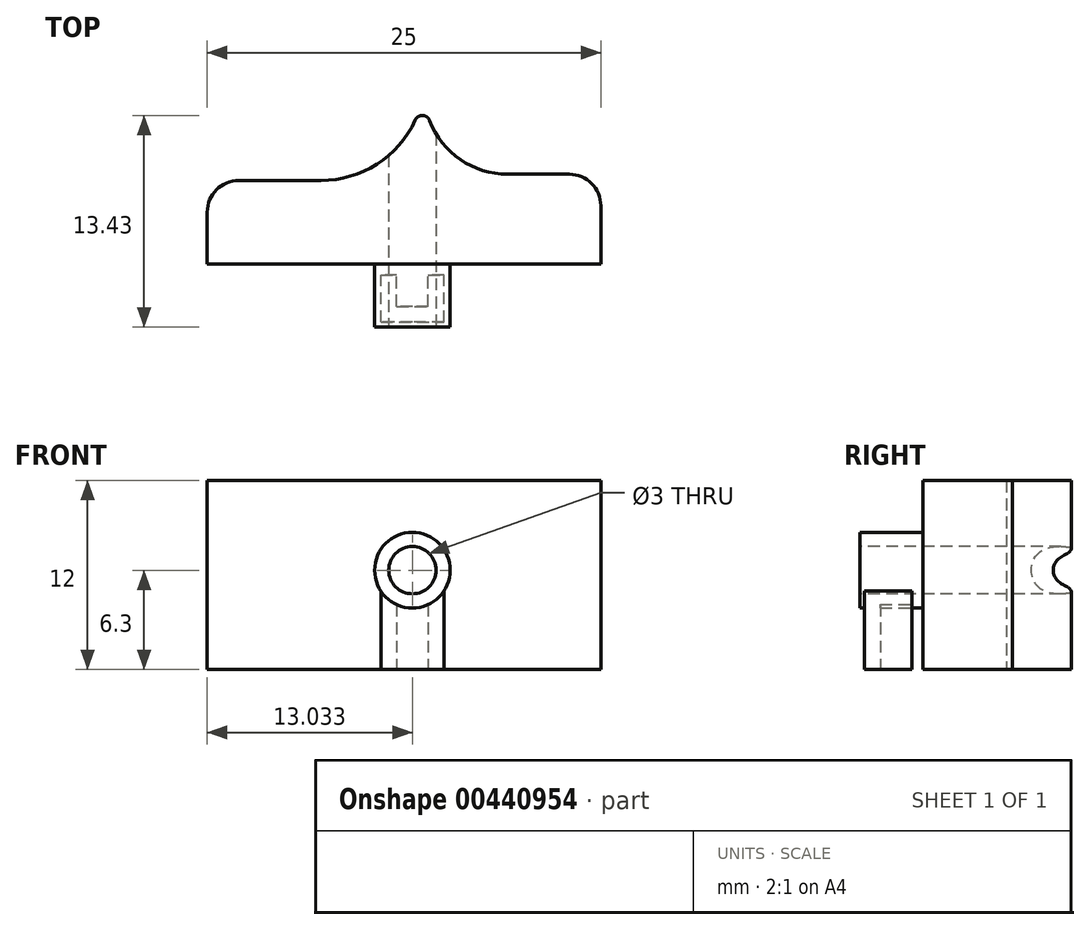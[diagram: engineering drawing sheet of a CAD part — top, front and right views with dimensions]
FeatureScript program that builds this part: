
annotation { "Feature Type Name" : "Feature", "Feature Type Description" : "" }
export const myFeature = defineFeature(function(context is Context, id is Id, definition is map)
    precondition{}
    {
        {
            var Q0;
            Q0=qCreatedBy(makeId("Top.planeOp"),FACE);
            var sketch = newSketch(context, id + "F0", { "sketchPlane" : qUnion([Q0])});
            skLineSegment(sketch, "E0", {"start": v(-35.12, 0) * mm, "end": v(42.7, 0) * mm});
            skLineSegment(sketch, "E1", {"start": v(47.98, 6) * mm, "end": v(-23.1, 6) * mm, "construction": true});
            skLineSegment(sketch, "E2", {"start": v(-19.18, 6.4) * mm, "end": v(41.17, 6.4) * mm, "construction": true});
            skCircle(sketch, "E3", {"center": v(6.58, 11.7) * mm, "radius": 5.3 * mm});
            skCircle(sketch, "E4", {"center": v(-5.28, 12.6) * mm, "radius": 6.6 * mm});
            skLineSegment(sketch, "E5.right", {"start": v(12.5, 6.4) * mm, "end": v(12.5, 0.7) * mm});
            skLineSegment(sketch, "E6.bottom", {"start": v(-11.88, 19.2) * mm, "end": v(11.88, 19.2) * mm, "construction": true});
            skLineSegment(sketch, "E6.left", {"start": v(-11.88, 19.2) * mm, "end": v(-11.88, 0) * mm, "construction": true});
            skLineSegment(sketch, "E6.right", {"start": v(11.88, 19.2) * mm, "end": v(11.88, 0) * mm, "construction": true});
            skLineSegment(sketch, "E7", {"start": v(0, 0) * mm, "end": v(0, 19.2) * mm, "construction": true});
            skLineSegment(sketch, "E8", {"start": v(-12.5, 0.7) * mm, "end": v(12.5, 0.7) * mm});
            skLineSegment(sketch, "E9", {"start": v(-12.5, 6) * mm, "end": v(-5.28, 6) * mm});
            skLineSegment(sketch, "E10", {"start": v(-12.5, 0.7) * mm, "end": v(-12.5, 6) * mm});
            skLineSegment(sketch, "E11", {"start": v(6.58, 6.4) * mm, "end": v(12.5, 6.4) * mm});
            skLineSegment(sketch, "E12", {"start": v(1.28, 19.2) * mm, "end": v(1.28, 0) * mm, "construction": true});
            skLineSegment(sketch, "E13", {"start": v(0.53, 19.2) * mm, "end": v(0.53, 0) * mm, "construction": true});
            skLineSegment(sketch, "E14.bottom", {"start": v(-0.47, -2) * mm, "end": v(1.53, -2) * mm});
            skLineSegment(sketch, "E14.top", {"start": v(-1.47, -3) * mm, "end": v(2.53, -3) * mm});
            skLineSegment(sketch, "E14.left", {"start": v(-1.47, -2) * mm, "end": v(-1.47, -3) * mm});
            skLineSegment(sketch, "E14.right", {"start": v(2.53, -2) * mm, "end": v(2.53, -3) * mm});
            skLineSegment(sketch, "E15.bottom", {"start": v(-1.47, 0.2) * mm, "end": v(-0.47, 0.2) * mm});
            skLineSegment(sketch, "E15.left", {"start": v(-1.47, 0.2) * mm, "end": v(-1.47, -2) * mm});
            skLineSegment(sketch, "E15.right", {"start": v(-0.47, 0.2) * mm, "end": v(-0.47, -2) * mm});
            skLineSegment(sketch, "E16.bottom", {"start": v(1.53, 0.2) * mm, "end": v(2.53, 0.2) * mm});
            skLineSegment(sketch, "E16.left", {"start": v(1.53, 0.2) * mm, "end": v(1.53, -2) * mm});
            skLineSegment(sketch, "E16.right", {"start": v(2.53, 0.2) * mm, "end": v(2.53, -2) * mm});
            skSolve(sketch);
        }
        {
            var Q0;
            Q0=makeQuery(id+"F0.imprint","IMPRINT",FACE,{"disambiguationData":[TD([[makeQuery(id+"F0.imprint","IMPRINT",EDGE,{"derivedFrom":sQuery(id+"F0.wireOp",EDGE,"E5.right")}),-1.0]])]});
            extrude(context, id + "F1", {"entities" : qUnion([Q0]), "depth" : 12 * mm});
        }
        {
            var Q0;
            Q0=makeQuery(id+"F1.opExtrude","SWEPT_FACE",FACE,{"disambiguationData":[OSD([sQuery(id+"F0.wireOp",EDGE,"E8")])]});
            var sketch = newSketch(context, id + "F2", { "sketchPlane" : qUnion([Q0])});
            skCircle(sketch, "E17", {"center": v(0.53, 6.3) * mm, "radius": 1.5 * mm});
            skLineSegment(sketch, "E18", {"start": v(-12.22, -4.4) * mm, "end": v(10.48, -4.4) * mm});
            skCircle(sketch, "E19", {"center": v(0.53, 6.3) * mm, "radius": 2.4 * mm});
            skLineSegment(sketch, "E20", {"start": v(0.53, 12) * mm, "end": v(0.53, 0) * mm, "construction": true});
            skSolve(sketch);
        }
        {
            var Q0;
            Q0=makeQuery(id+"F2.imprint","IMPRINT",FACE,{"disambiguationData":[TD([[makeQuery(id+"F2.imprint","IMPRINT",EDGE,{"derivedFrom":sQuery(id+"F2.wireOp",EDGE,"E17")}),1.0]])]});
            extrude(context, id + "F3", {"entities" : qUnion([Q0]), "operationType" : NewBodyOperationType.REMOVE, "oppositeDirection" : true, "depth" : 25 * mm});
        }
        {
            var Q0;
            {var subQ0=sQuery(id+"F0.wireOp",EDGE,"E3");var subQ1=sQuery(id+"F0.wireOp",EDGE,"E4");Q0=makeQuery(id+"F3.boolean.opBoolean","SPLIT",EDGE,{"disambiguationData":[TD([makeQuery(id+"F1.opExtrude","CAP_FACE",FACE,{"disambiguationData":[OSD([subQ0,subQ1,sQuery(id+"F0.wireOp",EDGE,"E5.right"),sQuery(id+"F0.wireOp",EDGE,"E8"),sQuery(id+"F0.wireOp",EDGE,"E9"),sQuery(id+"F0.wireOp",EDGE,"E10"),sQuery(id+"F0.wireOp",EDGE,"E11")])],"isStart":false})])],"derivedFrom":makeQuery(id+"F1.opExtrude","SWEPT_EDGE",EDGE,{"disambiguationData":[OSD([subQ0,subQ1])]})});}
            var Q1;
            {var subQ0=sQuery(id+"F0.wireOp",EDGE,"E3");var subQ1=sQuery(id+"F0.wireOp",EDGE,"E4");Q1=makeQuery(id+"F3.boolean.opBoolean","SPLIT",EDGE,{"disambiguationData":[TD([makeQuery(id+"F1.opExtrude","CAP_FACE",FACE,{"disambiguationData":[OSD([subQ0,subQ1,sQuery(id+"F0.wireOp",EDGE,"E5.right"),sQuery(id+"F0.wireOp",EDGE,"E8"),sQuery(id+"F0.wireOp",EDGE,"E9"),sQuery(id+"F0.wireOp",EDGE,"E10"),sQuery(id+"F0.wireOp",EDGE,"E11")])],"isStart":true})])],"derivedFrom":makeQuery(id+"F1.opExtrude","SWEPT_EDGE",EDGE,{"disambiguationData":[OSD([subQ0,subQ1])]})});}
            fillet(context, id + "F4", {"entities" : qUnion([Q0, Q1]), "radius" : 0.5 * mm, "tangentPropagation" : true, "allowEdgeOverflow" : false});
        }
        {
            var Q0;
            Q0=makeQuery(id+"F1.opExtrude","SWEPT_EDGE",EDGE,{"disambiguationData":[OSD([sQuery(id+"F0.wireOp",EDGE,"E9"),sQuery(id+"F0.wireOp",EDGE,"E10")])]});
            var Q1;
            Q1=makeQuery(id+"F1.opExtrude","SWEPT_EDGE",EDGE,{"disambiguationData":[OSD([sQuery(id+"F0.wireOp",EDGE,"E5.right"),sQuery(id+"F0.wireOp",EDGE,"E11")])]});
            fillet(context, id + "F5", {"entities" : qUnion([Q0, Q1]), "radius" : 2 * mm, "tangentPropagation" : true, "allowEdgeOverflow" : false});
        }
        {
            var Q0;
            Q0=makeQuery(id+"F2.imprint","IMPRINT",FACE,{"disambiguationData":[TD([[makeQuery(id+"F2.imprint","IMPRINT",EDGE,{"derivedFrom":sQuery(id+"F2.wireOp",EDGE,"E17")}),-1.0]])]});
            var Q1;
            {var subQ0=sQuery(id+"F2.wireOp",EDGE,"fL5psKod-5weR-QhTV-Rf9h-s4e1nVutnYcs.left");Q1=makeQuery(id+"F2.imprint","IMPRINT",FACE,{"disambiguationData":[TD([[makeQuery(id+"F2.imprint","IMPRINT",EDGE,{"derivedFrom":subQ0}),-1.0]])]});}
            extrude(context, id + "F6", {"entities" : qUnion([Q0, Q1]), "operationType" : NewBodyOperationType.ADD, "depth" : 4 * mm});
        }
        {
            var Q0;
            Q0=makeQuery(id+"F0.imprint","IMPRINT",FACE,{"disambiguationData":[TD([[makeQuery(id+"F0.imprint","IMPRINT",EDGE,{"derivedFrom":sQuery(id+"F0.wireOp",EDGE,"E14.bottom")}),-1.0]])]});
            var Q1;
            Q1=makeQuery(id+"F1.opExtrude","SWEPT_BODY",BODY,{"disambiguationData":[OSD([sQuery(id+"F0.wireOp",EDGE,"E3"),sQuery(id+"F0.wireOp",EDGE,"E4"),sQuery(id+"F0.wireOp",EDGE,"E5.right"),sQuery(id+"F0.wireOp",EDGE,"E8"),sQuery(id+"F0.wireOp",EDGE,"E9"),sQuery(id+"F0.wireOp",EDGE,"E10"),sQuery(id+"F0.wireOp",EDGE,"E11")])]});
            extrude(context, id + "F7", {"entities" : qUnion([Q0]), "operationType" : NewBodyOperationType.ADD, "endBound" : BoundingType.UP_TO_BODY, "endBoundEntityBody" : qUnion([Q1]), "depth" : 5 * mm});
        }
    });
